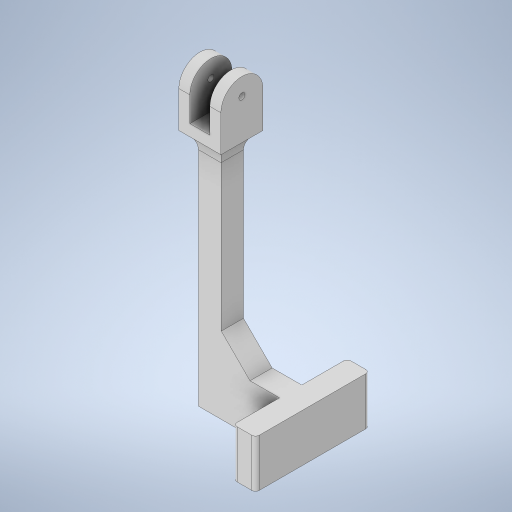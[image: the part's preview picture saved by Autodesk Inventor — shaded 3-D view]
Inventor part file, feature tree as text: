
AUTODESK INVENTOR PART (.ipt)
format: ipt  version: 2023 (Build 270158000, 158)  size: 321,024 bytes
history: native  units: mm
features: extrude x6, sketch x6, fillet x3, other x1, chamfer x1
ambient origin geometry x8: Origin, YZ Plane, XZ Plane, XY Plane, X Axis, Y Axis, Z Axis, Center Point
bodies: Body1 (feature_tree)
feature tree (17):
  other  "實體1"
  extrude  "擠出1"  Depth=12.0mm
  extrude  "擠出2"  Depth=11.6mm
  extrude  "擠出3"  Depth=125.0mm TaperAngle=0.0deg
  extrude  "擠出4"  Depth=25.0mm
  extrude  "擠出5"  Depth=30.5mm TaperAngle=0.0deg
  extrude  "擠出6"  Depth=25.0mm
  fillet  "圓角1"  Radius=59.6mm
  fillet  "圓角2"  Radius=23.8mm
  chamfer  "倒角1"  Distance=11.6mm
  fillet  "圓角3"  Radius=22.0mm
  sketch  "草圖1"
  sketch  "草圖2"
  sketch  "草圖3"
  sketch  "草圖4"
  sketch  "草圖5"
  sketch  "草圖6"
